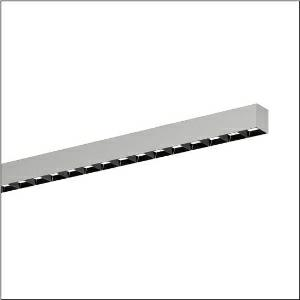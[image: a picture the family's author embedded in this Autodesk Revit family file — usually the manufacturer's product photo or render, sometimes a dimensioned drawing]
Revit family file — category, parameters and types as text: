
# Revit family: silica_r__21_51mx21dc3asb_b009
name_source: partatom
category: Lighting Fixtures
units: mm (PartAtom-declared; Revit-internal decimal feet)

## family parameters
Cut with Voids When Loaded = No
Host = Face
Light Source = No
Part Type = Normal
Room Calculation Point = No
Round Connector Dimension = Use Diameter
Shared = No

## types (1)
- --- (1 x LED, 10800 lm, 69.3 W, 3000K)
    Apparent Load = 69 VA
    CIE Flux Codes = 87 99 100 100 100
    Color Rendering = 80
    Color Temperature = 3000K
    Default Elevation = 1800 mm
    Description = Silica® 21, office luminaire, primary light control with darklight reflector, of PMMA, black, CAT 2 (L<= 3000cd/m²), light emission: direct distribution, primary light characteristic: symmetric, installation type: surface-mounted, LED, rated luminous flux: 10.800lm, luminous efficacy: 156lm/W, light colour: 830, colour temperature: 3000K, control gear: DALI 2, with terminal, 3+2-pole, max. 2.5mm², mains connection: 220..240V, AC, 50/60Hz, luminaire housing, of aluminium, metallic grey (RAL 9006), length: 3.004mm, width: 53mm, height: 53mm, protection rating (complete): IP20, insulation class (complete): insulation class I (protective earthing), certification: CE, permissible operating ambient temperature: 0..+35°C, standard: EN 50419, packaging unit: 1 piece
    Height = 53 mm
    Lamp = 1 x LED
    Lamp Light Flux = 10800 lm
    Lamp Power = 69.3 W
    Lamp count = 1
    Length = 3004 mm
    Luminous efficacy = 156 lm/W
    Manufacturer = Siteco
    ModVariant = No
    Model = 51MX21DC3ASB
    Mounting Place = Ceiling
    Mounting Type = Surface mounted
    Number of Poles = 1
    OnlyDefault = Yes
    Power Factor = 1
    Product Name = Silica® 21
    Product group = office luminaire | ceiling mounted
    ProductGroupID = 302
    Protection Class = Protection class I
    Protection Degree = IP 20
    RLX_Detail_Level = 1
    RLX_Emergency_Light_Flux = 0 lm
    RLX_Emergency_Type = 0
    RLX_Emergency_Type_DB = No
    RlxData = <blob elided: 63289 chars, md5=975c4936>
    Socket = socket
    Standby Power = 0 W
    System Light Flux = 10800 lm
    System Power = 69 W
    Type Comments = factory setting: luminous flux: 100 % | dim-lin: 254 | 393 mA
    Type Image = l_1335929.jpg
    URL = http://relux.com
    VarID = @adj_123496
    Voltage = 0 V
    Weight = 0.00 kg
    Width = 53 mm

## geometry (parser evidence)
native form markers: Blend x4, Sweep x11
no freeform markers — native parametric forms only
